# Revit family: Haworth_ComposeStorage_StackOn
name_source: partatom
category: Furniture Systems
revit_build: Autodesk Revit 2018 (Build: 20170223_1515(x64)
units: mm (PartAtom-declared; Revit-internal decimal feet)

## family parameters
Always vertical = Yes
Cut with Voids When Loaded = No
OmniClass Number = 23.40.70.14.64.21
OmniClass Title = Systems Furniture
Part Type = Normal
Room Calculation Point = No
Round Connector Dimension = Use Diameter
Shared = No
Work Plane-Based = No

## types (48) — shared parameters
# of Shelves = 2
Assembly Code = E2020200
Cabinet Finish = Haworth _ Wood _ White Oak
Custom Size = No
Description = Haworth - Compose Storage - Stack On
Door Finish = Haworth _ Wood _ White Oak
Manufacturer = Haworth
Max # of Shelves = 2
Max. Height = 55"
Max. Width = 36"
Min. Height = 19"
Min. Width = 30"
Min/Max Height = 19, 27, 31, 35, 39, 43, 47, 55 in.
Min/Max Width = 30, 36 in.
Model = BZxL
Revision Number = 5
Shelf 1 = Yes
Shelf 2 = Yes
Size = Verify Final Dim. w/ Haworth
Spacer Base = No
Spacer Height = 0"
Sustainability Info = http://media.haworth.com
URL = www.haworth.com
URL - Product = http://www.haworth.com
Warranty = http://www.haworth.com

## per-type parameters (varying)
| type | Actual Depth | Actual Height | Actual Width | Door Height | Door Width | Doors | Full Doors | Height | No Doors | Partial Doors | Shelf 1 Offset | Shelf 2 Offet | Width |
| 30w 19h - Full Doors | 15" | 19" | 30" | 19" | 15" | Yes | Yes | 19" | No | No | 6 21/256" | 6 21/256" | 30" |
| 30w 27h - Full Doors | 15" | 27" | 30" | 27" | 15" | Yes | Yes | 27" | No | No | 8 3/4" | 8 3/4" | 30" |
| 30w 31h - Full Doors | 15" | 31" | 30" | 31" | 15" | Yes | Yes | 31" | No | No | 10 21/256" | 10 21/256" | 30" |
| 30w 35h - Full Doors | 15" | 35" | 30" | 35" | 15" | Yes | Yes | 35" | No | No | 11 107/256" | 11 107/256" | 30" |
| 30w 39h - Full Doors | 15" | 39" | 30" | 39" | 15" | Yes | Yes | 39" | No | No | 12 3/4" | 12 3/4" | 30" |
| 30w 43h - Full Doors | 15" | 43" | 30" | 43" | 15" | Yes | Yes | 43" | No | No | 14 21/256" | 14 21/256" | 30" |
| 30w 47h - Full Doors | 15" | 47" | 30" | 47" | 15" | Yes | Yes | 47" | No | No | 15 107/256" | 15 107/256" | 30" |
| 30w 55h - Full Doors | 15" | 55" | 30" | 55" | 15" | Yes | Yes | 55" | No | No | 18 21/256" | 18 21/256" | 30" |
| 36w 19h - Full Doors | 15" | 19" | 36" | 19" | 18" | Yes | Yes | 19" | No | No | 6 21/256" | 6 21/256" | 36" |
| 36w 27h - Full Doors | 15" | 27" | 36" | 27" | 18" | Yes | Yes | 27" | No | No | 8 3/4" | 8 3/4" | 36" |
| 36w 31h - Full Doors | 15" | 31" | 36" | 31" | 18" | Yes | Yes | 31" | No | No | 10 21/256" | 10 21/256" | 36" |
| 36w 35h - Full Doors | 15" | 35" | 36" | 35" | 18" | Yes | Yes | 35" | No | No | 11 107/256" | 11 107/256" | 36" |
| 36w 39h - Full Doors | 15" | 39" | 36" | 39" | 18" | Yes | Yes | 39" | No | No | 12 3/4" | 12 3/4" | 36" |
| 36w 43h - Full Doors | 15" | 43" | 36" | 43" | 18" | Yes | Yes | 43" | No | No | 14 21/256" | 14 21/256" | 36" |
| 36w 47h - Full Doors | 15" | 47" | 36" | 47" | 18" | Yes | Yes | 47" | No | No | 15 107/256" | 15 107/256" | 36" |
| 36w 55h - Full Doors | 15" | 55" | 36" | 55" | 18" | Yes | Yes | 55" | No | No | 18 21/256" | 18 21/256" | 36" |
| 30w 19h - Partial Doors | 15" | 19" | 30" | 16" | 15" | Yes | No | 19" | No | Yes | 15 5/8" | 1 7/8" | 30" |
| 30w 27h - Partial Doors | 15" | 27" | 30" | 16" | 15" | Yes | No | 27" | No | Yes | 15 5/8" | 5 7/8" | 30" |
| 30w 31h - Partial Doors | 15" | 31" | 30" | 16" | 15" | Yes | No | 31" | No | Yes | 15 5/8" | 7 7/8" | 30" |
| 30w 35h - Partial Doors | 15" | 35" | 30" | 16" | 15" | Yes | No | 35" | No | Yes | 15 5/8" | 9 7/8" | 30" |
| 30w 39h - Partial Doors | 15" | 39" | 30" | 16" | 15" | Yes | No | 39" | No | Yes | 15 5/8" | 11 7/8" | 30" |
| 30w 43h - Partial Doors | 15" | 43" | 30" | 16" | 15" | Yes | No | 43" | No | Yes | 15 5/8" | 13 7/8" | 30" |
| 30w 47h - Partial Doors | 15" | 47" | 30" | 16" | 15" | Yes | No | 47" | No | Yes | 15 5/8" | 15 7/8" | 30" |
| 30w 55h - Partial Doors | 15" | 55" | 30" | 16" | 15" | Yes | No | 55" | No | Yes | 15 5/8" | 19 7/8" | 30" |
| 36w 19h - Partial Doors | 15" | 19" | 36" | 16" | 18" | Yes | No | 19" | No | Yes | 15 5/8" | 1 7/8" | 36" |
| 36w 27h - Partial Doors | 15" | 27" | 36" | 16" | 18" | Yes | No | 27" | No | Yes | 15 5/8" | 5 7/8" | 36" |
| 36w 31h - Partial Doors | 15" | 31" | 36" | 16" | 18" | Yes | No | 31" | No | Yes | 15 5/8" | 7 7/8" | 36" |
| 36w 35h - Partial Doors | 15" | 35" | 36" | 16" | 18" | Yes | No | 35" | No | Yes | 15 5/8" | 9 7/8" | 36" |
| 36w 39h - Partial Doors | 15" | 39" | 36" | 16" | 18" | Yes | No | 39" | No | Yes | 15 5/8" | 11 7/8" | 36" |
| 36w 43h - Partial Doors | 15" | 43" | 36" | 16" | 18" | Yes | No | 43" | No | Yes | 15 5/8" | 13 7/8" | 36" |
| 36w 47h - Partial Doors | 15" | 47" | 36" | 16" | 18" | Yes | No | 47" | No | Yes | 15 5/8" | 15 7/8" | 36" |
| 36w 55h - Partial Doors | 15" | 55" | 36" | 16" | 18" | Yes | No | 55" | No | Yes | 15 5/8" | 19 7/8" | 36" |
| 30w 19h - No Doors | 14 1/4" | 19" | 30" | 19" | 15" | No | No | 19" | Yes | No | 6 21/256" | 6 21/256" | 30" |
| 30w 27h - No Doors | 14 1/4" | 27" | 30" | 27" | 15" | No | No | 27" | Yes | No | 8 3/4" | 8 3/4" | 30" |
| 30w 31h - No Doors | 14 1/4" | 31" | 30" | 31" | 15" | No | No | 31" | Yes | No | 10 21/256" | 10 21/256" | 30" |
| 30w 35h - No Doors | 14 1/4" | 35" | 30" | 35" | 15" | No | No | 35" | Yes | No | 11 107/256" | 11 107/256" | 30" |
| 30w 39h - No Doors | 14 1/4" | 39" | 30" | 39" | 15" | No | No | 39" | Yes | No | 12 3/4" | 12 3/4" | 30" |
| 30w 43h - No Doors | 14 1/4" | 43" | 30" | 43" | 15" | No | No | 43" | Yes | No | 14 21/256" | 14 21/256" | 30" |
| 30w 47h - No Doors | 14 1/4" | 47" | 30" | 47" | 15" | No | No | 47" | Yes | No | 15 107/256" | 15 107/256" | 30" |
| 30w 55h - No Doors | 14 1/4" | 55" | 30" | 55" | 15" | No | No | 55" | Yes | No | 18 21/256" | 18 21/256" | 30" |
| 36w 19h - No Doors | 14 1/4" | 19" | 36" | 19" | 18" | No | No | 19" | Yes | No | 6 21/256" | 6 21/256" | 36" |
| 36w 27h - No Doors | 14 1/4" | 27" | 36" | 27" | 18" | No | No | 27" | Yes | No | 8 3/4" | 8 3/4" | 36" |
| 36w 31h - No Doors | 14 1/4" | 31" | 36" | 31" | 18" | No | No | 31" | Yes | No | 10 21/256" | 10 21/256" | 36" |
| 36w 35h - No Doors | 14 1/4" | 35" | 36" | 35" | 18" | No | No | 35" | Yes | No | 11 107/256" | 11 107/256" | 36" |
| 36w 39h - No Doors | 14 1/4" | 39" | 36" | 39" | 18" | No | No | 39" | Yes | No | 12 3/4" | 12 3/4" | 36" |
| 36w 43h - No Doors | 14 1/4" | 43" | 36" | 43" | 18" | No | No | 43" | Yes | No | 14 21/256" | 14 21/256" | 36" |
| 36w 47h - No Doors | 14 1/4" | 47" | 36" | 47" | 18" | No | No | 47" | Yes | No | 15 107/256" | 15 107/256" | 36" |
| 36w 55h - No Doors | 14 1/4" | 55" | 36" | 55" | 18" | No | No | 55" | Yes | No | 18 21/256" | 18 21/256" | 36" |

## geometry (parser evidence)
native form markers: Sweep x11
no freeform markers — native parametric forms only
